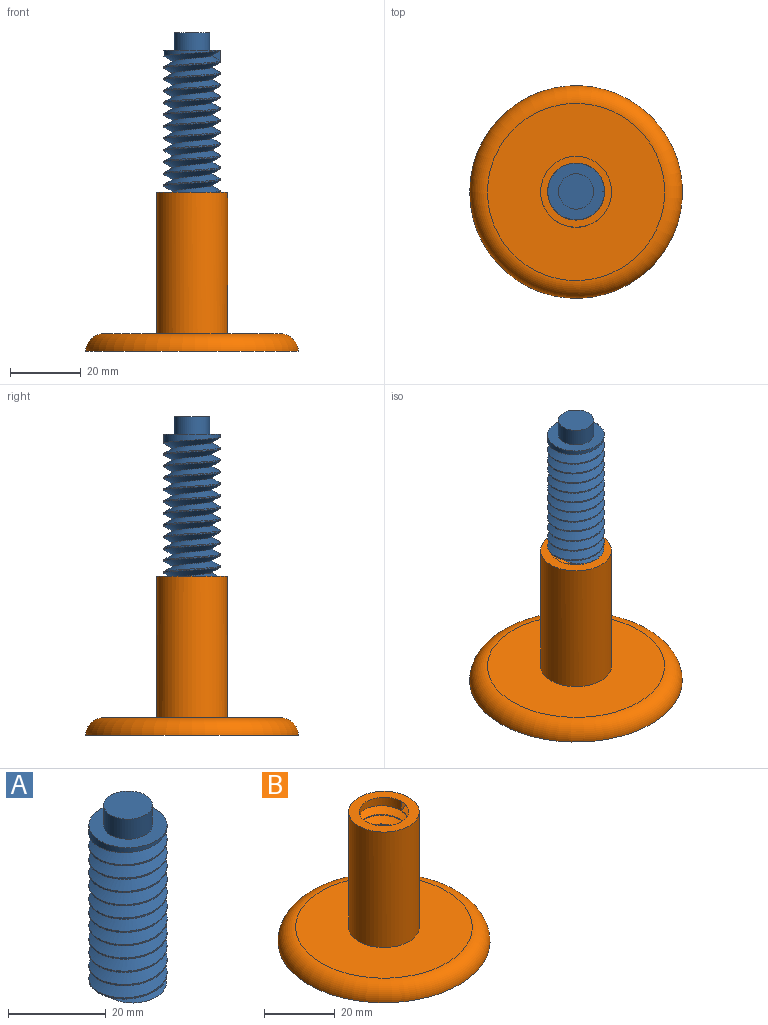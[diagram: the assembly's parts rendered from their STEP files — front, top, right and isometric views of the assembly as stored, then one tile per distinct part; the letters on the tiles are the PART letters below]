
ASSEMBLY  parts=2 mates=1
PART A: 8 faces, bbox 17.9x20.4x48.8 mm
  f0: cylinder r=8mm len=40mm, axis (0,0,-1), area 208.5mm2, adj f1,f2,f3,f4,f5
  f1: plane 16x16mm, normal (0,0,1), area 122.5mm2, adj f0,f6
  f2: plane 15.74x15.67mm, normal (0,0,-1), area 148.7mm2, adj f0,f3,f4
  f3: bspline ~41.5x18.48mm, area 1496.4mm2, adj f0,f2,f4,f5
  f4: bspline ~40.39x18.48mm, area 1430.5mm2, adj f0,f2,f3,f5
  f5: plane 3x2.6mm, normal (0,-1,0), area 3.9mm2, adj f0,f3,f4
  f6: cylinder r=5mm len=10mm, axis (0,0,-1), area 157.1mm2, adj f1,f7
  f7: plane 10x10mm, normal (0,0,1), area 78.5mm2, adj f6
PART B: 10 faces, bbox 64.9x64.9x48.6 mm
  f0: cylinder r=7mm len=40mm, axis (0,0,-1), area 182.4mm2, adj f2,f3,f4,f5,f8
  f1: cylinder r=10mm len=40mm, axis (0,0,-1), area 2513.3mm2, adj f2,f6
  f2: plane 20x20mm, normal (0,0,1), area 160.2mm2, adj f0,f1
  f3: bspline ~41.5x22.17mm, area 1841mm2, adj f0,f4,f5,f8
  f4: bspline ~40.39x22.17mm, area 1773.4mm2, adj f0,f3,f5,f8
  f5: plane 3x2.6mm, normal (0,-1,0), area 3.9mm2, adj f0,f3,f4
  f6: plane 50x50mm, normal (0,0,1), area 1649.3mm2, adj f1,f9
  f7: plane 60x60mm, normal (0,0,-1), area 2827.4mm2, adj f9
  f8: plane 16.43x16.41mm, normal (0,0,1), area 211.7mm2, adj f0,f3,f4
  f9: torus R=25mm, axis (0,0,-1), area 1390.8mm2, adj f6,f7
PLACE A t=(-22.7,-1.88,37.71)mm
PLACE B t=(-22.7,-1.88,-2.29)mm fixed
MATE cylindrical B.f1 <-> A.f0  axis (0,0,1) through (-22.7,-1.88,37.71)mm
